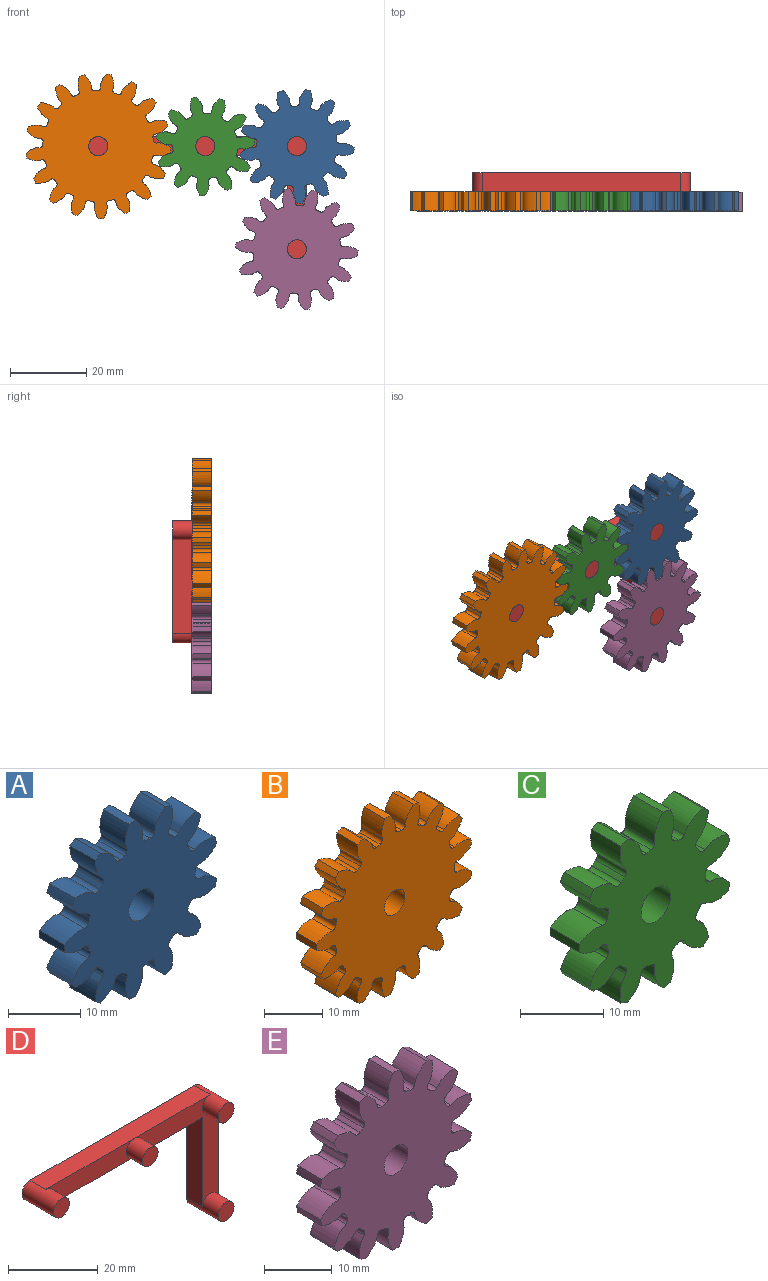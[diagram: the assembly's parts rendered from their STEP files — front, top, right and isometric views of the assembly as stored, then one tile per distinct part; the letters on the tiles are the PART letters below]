
ASSEMBLY  parts=5 mates=4
PART A: 81 faces, bbox 29.8x5x30 mm
  f0: extruded ~5x3.55mm, area 20.4mm2, adj f51,f52,f53,f54
  f1: cylinder r=10.5mm len=5mm, axis (0,1,0), area 4.2mm2, adj f52,f53,f54,f55
  f2: extruded ~5x3.55mm, area 20.4mm2, adj f3,f52,f53,f55
  f3: cylinder r=15mm len=5mm, axis (0,1,0), area 6.3mm2, adj f2,f4,f52,f53
  f4: extruded ~5x3.97mm, area 20.4mm2, adj f3,f52,f53,f56
  f5: cylinder r=10.5mm len=5mm, axis (0,1,0), area 4.2mm2, adj f52,f53,f56,f57
  f6: extruded ~5x3.23mm, area 20.4mm2, adj f7,f52,f53,f57
  f7: cylinder r=15mm len=5mm, axis (0,1,0), area 6.3mm2, adj f6,f8,f52,f53
  f8: extruded ~5x3.49mm, area 20.4mm2, adj f7,f52,f53,f58
  f9: cylinder r=10.5mm len=5mm, axis (0,1,0), area 4.2mm2, adj f52,f53,f58,f59
  f10: extruded ~5x3.94mm, area 20.4mm2, adj f11,f52,f53,f59
  f11: cylinder r=15mm len=5mm, axis (0,1,0), area 6.3mm2, adj f10,f12,f52,f53
  f12: extruded ~5x3.31mm, area 20.4mm2, adj f11,f52,f53,f60
  f13: cylinder r=10.5mm len=5mm, axis (0,1,0), area 4.2mm2, adj f52,f53,f60,f61
  f14: extruded ~5x3.74mm, area 20.4mm2, adj f15,f52,f53,f61
  f15: cylinder r=15mm len=5mm, axis (0,1,0), area 6.3mm2, adj f14,f16,f52,f53
  f16: extruded ~5x3.95mm, area 20.4mm2, adj f15,f52,f53,f62
  f17: cylinder r=10.5mm len=5mm, axis (0,1,0), area 4.2mm2, adj f52,f53,f62,f63
  f18: extruded ~5x2.93mm, area 20.4mm2, adj f19,f52,f53,f63
  f19: cylinder r=15mm len=5mm, axis (0,1,0), area 6.3mm2, adj f18,f20,f52,f53
  f20: extruded ~5x3.69mm, area 20.4mm2, adj f19,f52,f53,f64
  f21: cylinder r=10.5mm len=5mm, axis (0,1,0), area 4.2mm2, adj f52,f53,f64,f65
  f22: extruded ~5x3.84mm, area 20.4mm2, adj f23,f52,f53,f65
  f23: cylinder r=15mm len=5mm, axis (0,1,0), area 6.3mm2, adj f22,f24,f52,f53
  f24: extruded ~5x3.02mm, area 20.4mm2, adj f23,f52,f53,f66
  f25: cylinder r=10.5mm len=5mm, axis (0,1,0), area 4.2mm2, adj f52,f53,f66,f67
  f26: extruded ~5x3.87mm, area 20.4mm2, adj f27,f52,f53,f67
  f27: cylinder r=15mm len=5mm, axis (0,1,0), area 6.3mm2, adj f26,f28,f52,f53
  f28: extruded ~5x3.87mm, area 20.4mm2, adj f27,f52,f53,f68
  f29: cylinder r=10.5mm len=5mm, axis (0,1,0), area 4.2mm2, adj f52,f53,f68,f69
  f30: extruded ~5x3.02mm, area 20.4mm2, adj f31,f52,f53,f69
  f31: cylinder r=15mm len=5mm, axis (0,1,0), area 6.3mm2, adj f30,f32,f52,f53
  f32: extruded ~5x3.84mm, area 20.4mm2, adj f31,f52,f53,f70
  f33: cylinder r=10.5mm len=5mm, axis (0,1,0), area 4.2mm2, adj f52,f53,f70,f71
  f34: extruded ~5x3.69mm, area 20.4mm2, adj f35,f52,f53,f71
  f35: cylinder r=15mm len=5mm, axis (0,1,0), area 6.3mm2, adj f34,f36,f52,f53
  f36: extruded ~5x2.93mm, area 20.4mm2, adj f35,f52,f53,f72
  f37: cylinder r=10.5mm len=5mm, axis (0,1,0), area 4.2mm2, adj f52,f53,f72,f73
  f38: extruded ~5x3.95mm, area 20.4mm2, adj f39,f52,f53,f73
  f39: cylinder r=15mm len=5mm, axis (0,1,0), area 6.3mm2, adj f38,f40,f52,f53
  f40: extruded ~5x3.74mm, area 20.4mm2, adj f39,f52,f53,f74
  f41: cylinder r=10.5mm len=5mm, axis (0,1,0), area 4.2mm2, adj f52,f53,f74,f75
  f42: extruded ~5x3.31mm, area 20.4mm2, adj f43,f52,f53,f75
  f43: cylinder r=15mm len=5mm, axis (0,1,0), area 6.3mm2, adj f42,f44,f52,f53
  f44: extruded ~5x3.94mm, area 20.4mm2, adj f43,f52,f53,f76
  f45: cylinder r=10.5mm len=5mm, axis (0,1,0), area 4.2mm2, adj f52,f53,f76,f77
  f46: extruded ~5x3.49mm, area 20.4mm2, adj f47,f52,f53,f77
  f47: cylinder r=15mm len=5mm, axis (0,1,0), area 6.3mm2, adj f46,f48,f52,f53
  f48: extruded ~5x3.23mm, area 20.4mm2, adj f47,f52,f53,f78
  f49: cylinder r=10.5mm len=5mm, axis (0,1,0), area 4.2mm2, adj f52,f53,f78,f79
  f50: extruded ~5x3.97mm, area 20.4mm2, adj f51,f52,f53,f79
  f51: cylinder r=15mm len=5mm, axis (0,1,0), area 6.3mm2, adj f0,f50,f52,f53
  f52: plane 29.98x29.76mm, normal (0,-1,0), area 492.7mm2, adj f0,f1,f2,f3,f4,f5,f6,f7
  f53: plane 29.98x29.76mm, normal (0,1,0), area 492.7mm2, adj f0,f1,f2,f3,f4,f5,f6,f7
  f54: cylinder r=0.74mm len=5mm, axis (0,1,0), area 5.6mm2, adj f0,f1,f52,f53
  f55: cylinder r=0.74mm len=5mm, axis (0,1,0), area 5.6mm2, adj f1,f2,f52,f53
  f56: cylinder r=0.74mm len=5mm, axis (0,1,0), area 5.6mm2, adj f4,f5,f52,f53
  f57: cylinder r=0.74mm len=5mm, axis (0,1,0), area 5.6mm2, adj f5,f6,f52,f53
  f58: cylinder r=0.74mm len=5mm, axis (0,1,0), area 5.6mm2, adj f8,f9,f52,f53
  f59: cylinder r=0.74mm len=5mm, axis (0,1,0), area 5.6mm2, adj f9,f10,f52,f53
  f60: cylinder r=0.74mm len=5mm, axis (0,1,0), area 5.6mm2, adj f12,f13,f52,f53
  f61: cylinder r=0.74mm len=5mm, axis (0,1,0), area 5.6mm2, adj f13,f14,f52,f53
  f62: cylinder r=0.74mm len=5mm, axis (0,1,0), area 5.6mm2, adj f16,f17,f52,f53
  f63: cylinder r=0.74mm len=5mm, axis (0,1,0), area 5.6mm2, adj f17,f18,f52,f53
  f64: cylinder r=0.74mm len=5mm, axis (0,1,0), area 5.6mm2, adj f20,f21,f52,f53
  f65: cylinder r=0.74mm len=5mm, axis (0,1,0), area 5.6mm2, adj f21,f22,f52,f53
  f66: cylinder r=0.74mm len=5mm, axis (0,1,0), area 5.6mm2, adj f24,f25,f52,f53
  f67: cylinder r=0.74mm len=5mm, axis (0,1,0), area 5.6mm2, adj f25,f26,f52,f53
  f68: cylinder r=0.74mm len=5mm, axis (0,1,0), area 5.6mm2, adj f28,f29,f52,f53
  f69: cylinder r=0.74mm len=5mm, axis (0,1,0), area 5.6mm2, adj f29,f30,f52,f53
  f70: cylinder r=0.74mm len=5mm, axis (0,1,0), area 5.6mm2, adj f32,f33,f52,f53
  f71: cylinder r=0.74mm len=5mm, axis (0,1,0), area 5.6mm2, adj f33,f34,f52,f53
  f72: cylinder r=0.74mm len=5mm, axis (0,1,0), area 5.6mm2, adj f36,f37,f52,f53
  f73: cylinder r=0.74mm len=5mm, axis (0,1,0), area 5.6mm2, adj f37,f38,f52,f53
  f74: cylinder r=0.74mm len=5mm, axis (0,1,0), area 5.6mm2, adj f40,f41,f52,f53
  f75: cylinder r=0.74mm len=5mm, axis (0,1,0), area 5.6mm2, adj f41,f42,f52,f53
  f76: cylinder r=0.74mm len=5mm, axis (0,1,0), area 5.6mm2, adj f44,f45,f52,f53
  f77: cylinder r=0.74mm len=5mm, axis (0,1,0), area 5.6mm2, adj f45,f46,f52,f53
  f78: cylinder r=0.74mm len=5mm, axis (0,1,0), area 5.6mm2, adj f48,f49,f52,f53
  f79: cylinder r=0.74mm len=5mm, axis (0,1,0), area 5.6mm2, adj f49,f50,f52,f53
  f80: cylinder r=2.5mm len=5mm, axis (0,1,0), area 78.5mm2, adj f52,f53
PART B: 105 faces, bbox 37.8x5x38 mm
  f0: extruded ~5x3.6mm, area 20.3mm2, adj f67,f68,f69,f70
  f1: cylinder r=14.5mm len=5mm, axis (0,1,0), area 4.1mm2, adj f68,f69,f70,f71
  f2: extruded ~5x3.6mm, area 20.3mm2, adj f3,f68,f69,f71
  f3: cylinder r=19mm len=5mm, axis (0,1,0), area 6.7mm2, adj f2,f4,f68,f69
  f4: extruded ~5x3.96mm, area 20.3mm2, adj f3,f68,f69,f72
  f5: cylinder r=14.5mm len=5mm, axis (0,1,0), area 4.1mm2, adj f68,f69,f72,f73
  f6: extruded ~5x2.84mm, area 20.3mm2, adj f7,f68,f69,f73
  f7: cylinder r=19mm len=5mm, axis (0,1,0), area 6.7mm2, adj f6,f8,f68,f69
  f8: extruded ~5x3.77mm, area 20.3mm2, adj f7,f68,f69,f74
  f9: cylinder r=14.5mm len=5mm, axis (0,1,0), area 4.1mm2, adj f68,f69,f74,f75
  f10: extruded ~5x3.65mm, area 20.3mm2, adj f11,f68,f69,f75
  f11: cylinder r=19mm len=5mm, axis (0,1,0), area 6.7mm2, adj f10,f12,f68,f69
  f12: extruded ~5x3.08mm, area 20.3mm2, adj f11,f68,f69,f76
  f13: cylinder r=14.5mm len=5mm, axis (0,1,0), area 4.1mm2, adj f68,f69,f76,f77
  f14: extruded ~5x3.96mm, area 20.3mm2, adj f15,f68,f69,f77
  f15: cylinder r=19mm len=5mm, axis (0,1,0), area 6.7mm2, adj f14,f16,f68,f69
  f16: extruded ~5x3.44mm, area 20.3mm2, adj f15,f68,f69,f78
  f17: cylinder r=14.5mm len=5mm, axis (0,1,0), area 4.1mm2, adj f68,f69,f78,f79
  f18: extruded ~5x3.74mm, area 20.3mm2, adj f19,f68,f69,f79
  f19: cylinder r=19mm len=5mm, axis (0,1,0), area 6.7mm2, adj f18,f20,f68,f69
  f20: extruded ~5x3.92mm, area 20.3mm2, adj f19,f68,f69,f80
  f21: cylinder r=14.5mm len=5mm, axis (0,1,0), area 4.1mm2, adj f68,f69,f80,f81
  f22: extruded ~5x3.01mm, area 20.3mm2, adj f23,f68,f69,f81
  f23: cylinder r=19mm len=5mm, axis (0,1,0), area 6.7mm2, adj f22,f24,f68,f69
  f24: extruded ~5x3.87mm, area 20.3mm2, adj f23,f68,f69,f82
  f25: cylinder r=14.5mm len=5mm, axis (0,1,0), area 4.1mm2, adj f68,f69,f82,f83
  f26: extruded ~5x3.49mm, area 20.3mm2, adj f27,f68,f69,f83
  f27: cylinder r=19mm len=5mm, axis (0,1,0), area 6.7mm2, adj f26,f28,f68,f69
  f28: extruded ~5x3.3mm, area 20.3mm2, adj f27,f68,f69,f84
  f29: cylinder r=14.5mm len=5mm, axis (0,1,0), area 4.1mm2, adj f68,f69,f84,f85
  f30: extruded ~5x3.93mm, area 20.3mm2, adj f31,f68,f69,f85
  f31: cylinder r=19mm len=5mm, axis (0,1,0), area 6.7mm2, adj f30,f32,f68,f69
  f32: extruded ~5x3.24mm, area 20.3mm2, adj f31,f68,f69,f86
  f33: cylinder r=14.5mm len=5mm, axis (0,1,0), area 4.1mm2, adj f68,f69,f86,f87
  f34: extruded ~5x3.84mm, area 20.3mm2, adj f35,f68,f69,f87
  f35: cylinder r=19mm len=5mm, axis (0,1,0), area 6.7mm2, adj f34,f36,f68,f69
  f36: extruded ~5x3.84mm, area 20.3mm2, adj f35,f68,f69,f88
  f37: cylinder r=14.5mm len=5mm, axis (0,1,0), area 4.1mm2, adj f68,f69,f88,f89
  f38: extruded ~5x3.24mm, area 20.3mm2, adj f39,f68,f69,f89
  f39: cylinder r=19mm len=5mm, axis (0,1,0), area 6.7mm2, adj f38,f40,f68,f69
  f40: extruded ~5x3.93mm, area 20.3mm2, adj f39,f68,f69,f90
  f41: cylinder r=14.5mm len=5mm, axis (0,1,0), area 4.1mm2, adj f68,f69,f90,f91
  f42: extruded ~5x3.3mm, area 20.3mm2, adj f43,f68,f69,f91
  f43: cylinder r=19mm len=5mm, axis (0,1,0), area 6.7mm2, adj f42,f44,f68,f69
  f44: extruded ~5x3.49mm, area 20.3mm2, adj f43,f68,f69,f92
  f45: cylinder r=14.5mm len=5mm, axis (0,1,0), area 4.1mm2, adj f68,f69,f92,f93
  f46: extruded ~5x3.87mm, area 20.3mm2, adj f47,f68,f69,f93
  f47: cylinder r=19mm len=5mm, axis (0,1,0), area 6.7mm2, adj f46,f48,f68,f69
  f48: extruded ~5x3.01mm, area 20.3mm2, adj f47,f68,f69,f94
  f49: cylinder r=14.5mm len=5mm, axis (0,1,0), area 4.1mm2, adj f68,f69,f94,f95
  f50: extruded ~5x3.92mm, area 20.3mm2, adj f51,f68,f69,f95
  f51: cylinder r=19mm len=5mm, axis (0,1,0), area 6.7mm2, adj f50,f52,f68,f69
  f52: extruded ~5x3.74mm, area 20.3mm2, adj f51,f68,f69,f96
  f53: cylinder r=14.5mm len=5mm, axis (0,1,0), area 4.1mm2, adj f68,f69,f96,f97
  f54: extruded ~5x3.44mm, area 20.3mm2, adj f55,f68,f69,f97
  f55: cylinder r=19mm len=5mm, axis (0,1,0), area 6.7mm2, adj f54,f56,f68,f69
  f56: extruded ~5x3.96mm, area 20.3mm2, adj f55,f68,f69,f98
  f57: cylinder r=14.5mm len=5mm, axis (0,1,0), area 4.1mm2, adj f68,f69,f98,f99
  f58: extruded ~5x3.08mm, area 20.3mm2, adj f59,f68,f69,f99
  f59: cylinder r=19mm len=5mm, axis (0,1,0), area 6.7mm2, adj f58,f60,f68,f69
  f60: extruded ~5x3.65mm, area 20.3mm2, adj f59,f68,f69,f100
  f61: cylinder r=14.5mm len=5mm, axis (0,1,0), area 4.1mm2, adj f68,f69,f100,f101
  f62: extruded ~5x3.77mm, area 20.3mm2, adj f63,f68,f69,f101
  f63: cylinder r=19mm len=5mm, axis (0,1,0), area 6.7mm2, adj f62,f64,f68,f69
  f64: extruded ~5x2.84mm, area 20.3mm2, adj f63,f68,f69,f102
  f65: cylinder r=14.5mm len=5mm, axis (0,1,0), area 4.1mm2, adj f68,f69,f102,f103
  f66: extruded ~5x3.96mm, area 20.3mm2, adj f67,f68,f69,f103
  f67: cylinder r=19mm len=5mm, axis (0,1,0), area 6.7mm2, adj f0,f66,f68,f69
  f68: plane 37.98x37.82mm, normal (0,-1,0), area 865mm2, adj f0,f1,f2,f3,f4,f5,f6,f7
  f69: plane 37.98x37.82mm, normal (0,1,0), area 865mm2, adj f0,f1,f2,f3,f4,f5,f6,f7
  f70: cylinder r=0.75mm len=5mm, axis (0,1,0), area 5.7mm2, adj f0,f1,f68,f69
  f71: cylinder r=0.75mm len=5mm, axis (0,1,0), area 5.7mm2, adj f1,f2,f68,f69
  f72: cylinder r=0.75mm len=5mm, axis (0,1,0), area 5.7mm2, adj f4,f5,f68,f69
  f73: cylinder r=0.75mm len=5mm, axis (0,1,0), area 5.7mm2, adj f5,f6,f68,f69
  f74: cylinder r=0.75mm len=5mm, axis (0,1,0), area 5.7mm2, adj f8,f9,f68,f69
  f75: cylinder r=0.75mm len=5mm, axis (0,1,0), area 5.7mm2, adj f9,f10,f68,f69
  f76: cylinder r=0.75mm len=5mm, axis (0,1,0), area 5.7mm2, adj f12,f13,f68,f69
  f77: cylinder r=0.75mm len=5mm, axis (0,1,0), area 5.7mm2, adj f13,f14,f68,f69
  f78: cylinder r=0.75mm len=5mm, axis (0,1,0), area 5.7mm2, adj f16,f17,f68,f69
  f79: cylinder r=0.75mm len=5mm, axis (0,1,0), area 5.7mm2, adj f17,f18,f68,f69
  f80: cylinder r=0.75mm len=5mm, axis (0,1,0), area 5.7mm2, adj f20,f21,f68,f69
  f81: cylinder r=0.75mm len=5mm, axis (0,1,0), area 5.7mm2, adj f21,f22,f68,f69
  f82: cylinder r=0.75mm len=5mm, axis (0,1,0), area 5.7mm2, adj f24,f25,f68,f69
  f83: cylinder r=0.75mm len=5mm, axis (0,1,0), area 5.7mm2, adj f25,f26,f68,f69
  f84: cylinder r=0.75mm len=5mm, axis (0,1,0), area 5.7mm2, adj f28,f29,f68,f69
  f85: cylinder r=0.75mm len=5mm, axis (0,1,0), area 5.7mm2, adj f29,f30,f68,f69
  f86: cylinder r=0.75mm len=5mm, axis (0,1,0), area 5.7mm2, adj f32,f33,f68,f69
  f87: cylinder r=0.75mm len=5mm, axis (0,1,0), area 5.7mm2, adj f33,f34,f68,f69
  f88: cylinder r=0.75mm len=5mm, axis (0,1,0), area 5.7mm2, adj f36,f37,f68,f69
  f89: cylinder r=0.75mm len=5mm, axis (0,1,0), area 5.7mm2, adj f37,f38,f68,f69
  f90: cylinder r=0.75mm len=5mm, axis (0,1,0), area 5.7mm2, adj f40,f41,f68,f69
  f91: cylinder r=0.75mm len=5mm, axis (0,1,0), area 5.7mm2, adj f41,f42,f68,f69
  f92: cylinder r=0.75mm len=5mm, axis (0,1,0), area 5.7mm2, adj f44,f45,f68,f69
  f93: cylinder r=0.75mm len=5mm, axis (0,1,0), area 5.7mm2, adj f45,f46,f68,f69
  f94: cylinder r=0.75mm len=5mm, axis (0,1,0), area 5.7mm2, adj f48,f49,f68,f69
  f95: cylinder r=0.75mm len=5mm, axis (0,1,0), area 5.7mm2, adj f49,f50,f68,f69
  f96: cylinder r=0.75mm len=5mm, axis (0,1,0), area 5.7mm2, adj f52,f53,f68,f69
  f97: cylinder r=0.75mm len=5mm, axis (0,1,0), area 5.7mm2, adj f53,f54,f68,f69
  f98: cylinder r=0.75mm len=5mm, axis (0,1,0), area 5.7mm2, adj f56,f57,f68,f69
  f99: cylinder r=0.75mm len=5mm, axis (0,1,0), area 5.7mm2, adj f57,f58,f68,f69
  f100: cylinder r=0.75mm len=5mm, axis (0,1,0), area 5.7mm2, adj f60,f61,f68,f69
  f101: cylinder r=0.75mm len=5mm, axis (0,1,0), area 5.7mm2, adj f61,f62,f68,f69
  f102: cylinder r=0.75mm len=5mm, axis (0,1,0), area 5.7mm2, adj f64,f65,f68,f69
  f103: cylinder r=0.75mm len=5mm, axis (0,1,0), area 5.7mm2, adj f65,f66,f68,f69
  f104: cylinder r=2.5mm len=5mm, axis (0,1,0), area 78.5mm2, adj f68,f69
PART C: 69 faces, bbox 25.7x5x26 mm
  f0: extruded ~5x3.51mm, area 20.6mm2, adj f43,f44,f45,f46
  f1: cylinder r=8.5mm len=5mm, axis (0,1,0), area 4.2mm2, adj f44,f45,f46,f47
  f2: extruded ~5x3.51mm, area 20.6mm2, adj f3,f44,f45,f47
  f3: cylinder r=13mm len=5mm, axis (0,1,0), area 6mm2, adj f2,f4,f44,f45
  f4: extruded ~5x3.98mm, area 20.6mm2, adj f3,f44,f45,f48
  f5: cylinder r=8.5mm len=5mm, axis (0,1,0), area 4.2mm2, adj f44,f45,f48,f49
  f6: extruded ~5x3.5mm, area 20.6mm2, adj f7,f44,f45,f49
  f7: cylinder r=13mm len=5mm, axis (0,1,0), area 6mm2, adj f6,f8,f44,f45
  f8: extruded ~5x3.19mm, area 20.6mm2, adj f7,f44,f45,f50
  f9: cylinder r=8.5mm len=5mm, axis (0,1,0), area 4.2mm2, adj f44,f45,f50,f51
  f10: extruded ~5x3.98mm, area 20.6mm2, adj f11,f44,f45,f51
  f11: cylinder r=13mm len=5mm, axis (0,1,0), area 6mm2, adj f10,f12,f44,f45
  f12: extruded ~5x3.75mm, area 20.6mm2, adj f11,f44,f45,f52
  f13: cylinder r=8.5mm len=5mm, axis (0,1,0), area 4.2mm2, adj f44,f45,f52,f53
  f14: extruded ~5x3.2mm, area 20.6mm2, adj f15,f44,f45,f53
  f15: cylinder r=13mm len=5mm, axis (0,1,0), area 6mm2, adj f14,f16,f44,f45
  f16: extruded ~5x3.9mm, area 20.6mm2, adj f15,f44,f45,f54
  f17: cylinder r=8.5mm len=5mm, axis (0,1,0), area 4.2mm2, adj f44,f45,f54,f55
  f18: extruded ~5x3.74mm, area 20.6mm2, adj f19,f44,f45,f55
  f19: cylinder r=13mm len=5mm, axis (0,1,0), area 6mm2, adj f18,f20,f44,f45
  f20: extruded ~5x2.83mm, area 20.6mm2, adj f19,f44,f45,f56
  f21: cylinder r=8.5mm len=5mm, axis (0,1,0), area 4.2mm2, adj f44,f45,f56,f57
  f22: extruded ~5x3.9mm, area 20.6mm2, adj f23,f44,f45,f57
  f23: cylinder r=13mm len=5mm, axis (0,1,0), area 6mm2, adj f22,f24,f44,f45
  f24: extruded ~5x3.9mm, area 20.6mm2, adj f23,f44,f45,f58
  f25: cylinder r=8.5mm len=5mm, axis (0,1,0), area 4.2mm2, adj f44,f45,f58,f59
  f26: extruded ~5x2.83mm, area 20.6mm2, adj f27,f44,f45,f59
  f27: cylinder r=13mm len=5mm, axis (0,1,0), area 6mm2, adj f26,f28,f44,f45
  f28: extruded ~5x3.74mm, area 20.6mm2, adj f27,f44,f45,f60
  f29: cylinder r=8.5mm len=5mm, axis (0,1,0), area 4.2mm2, adj f44,f45,f60,f61
  f30: extruded ~5x3.9mm, area 20.6mm2, adj f31,f44,f45,f61
  f31: cylinder r=13mm len=5mm, axis (0,1,0), area 6mm2, adj f30,f32,f44,f45
  f32: extruded ~5x3.2mm, area 20.6mm2, adj f31,f44,f45,f62
  f33: cylinder r=8.5mm len=5mm, axis (0,1,0), area 4.2mm2, adj f44,f45,f62,f63
  f34: extruded ~5x3.75mm, area 20.6mm2, adj f35,f44,f45,f63
  f35: cylinder r=13mm len=5mm, axis (0,1,0), area 6mm2, adj f34,f36,f44,f45
  f36: extruded ~5x3.98mm, area 20.6mm2, adj f35,f44,f45,f64
  f37: cylinder r=8.5mm len=5mm, axis (0,1,0), area 4.2mm2, adj f44,f45,f64,f65
  f38: extruded ~5x3.19mm, area 20.6mm2, adj f39,f44,f45,f65
  f39: cylinder r=13mm len=5mm, axis (0,1,0), area 6mm2, adj f38,f40,f44,f45
  f40: extruded ~5x3.5mm, area 20.6mm2, adj f39,f44,f45,f66
  f41: cylinder r=8.5mm len=5mm, axis (0,1,0), area 4.2mm2, adj f44,f45,f66,f67
  f42: extruded ~5x3.98mm, area 20.6mm2, adj f43,f44,f45,f67
  f43: cylinder r=13mm len=5mm, axis (0,1,0), area 6mm2, adj f0,f42,f44,f45
  f44: plane 25.96x25.7mm, normal (0,-1,0), area 344.7mm2, adj f0,f1,f2,f3,f4,f5,f6,f7
  f45: plane 25.96x25.7mm, normal (0,1,0), area 344.7mm2, adj f0,f1,f2,f3,f4,f5,f6,f7
  f46: cylinder r=0.72mm len=5mm, axis (0,1,0), area 5.4mm2, adj f0,f1,f44,f45
  f47: cylinder r=0.72mm len=5mm, axis (0,1,0), area 5.4mm2, adj f1,f2,f44,f45
  f48: cylinder r=0.72mm len=5mm, axis (0,1,0), area 5.4mm2, adj f4,f5,f44,f45
  f49: cylinder r=0.72mm len=5mm, axis (0,1,0), area 5.4mm2, adj f5,f6,f44,f45
  f50: cylinder r=0.72mm len=5mm, axis (0,1,0), area 5.4mm2, adj f8,f9,f44,f45
  f51: cylinder r=0.72mm len=5mm, axis (0,1,0), area 5.4mm2, adj f9,f10,f44,f45
  f52: cylinder r=0.72mm len=5mm, axis (0,1,0), area 5.4mm2, adj f12,f13,f44,f45
  f53: cylinder r=0.72mm len=5mm, axis (0,1,0), area 5.4mm2, adj f13,f14,f44,f45
  f54: cylinder r=0.72mm len=5mm, axis (0,1,0), area 5.4mm2, adj f16,f17,f44,f45
  f55: cylinder r=0.72mm len=5mm, axis (0,1,0), area 5.4mm2, adj f17,f18,f44,f45
  f56: cylinder r=0.72mm len=5mm, axis (0,1,0), area 5.4mm2, adj f20,f21,f44,f45
  f57: cylinder r=0.72mm len=5mm, axis (0,1,0), area 5.4mm2, adj f21,f22,f44,f45
  f58: cylinder r=0.72mm len=5mm, axis (0,1,0), area 5.4mm2, adj f24,f25,f44,f45
  f59: cylinder r=0.72mm len=5mm, axis (0,1,0), area 5.4mm2, adj f25,f26,f44,f45
  f60: cylinder r=0.72mm len=5mm, axis (0,1,0), area 5.4mm2, adj f28,f29,f44,f45
  f61: cylinder r=0.72mm len=5mm, axis (0,1,0), area 5.4mm2, adj f29,f30,f44,f45
  f62: cylinder r=0.72mm len=5mm, axis (0,1,0), area 5.4mm2, adj f32,f33,f44,f45
  f63: cylinder r=0.72mm len=5mm, axis (0,1,0), area 5.4mm2, adj f33,f34,f44,f45
  f64: cylinder r=0.72mm len=5mm, axis (0,1,0), area 5.4mm2, adj f36,f37,f44,f45
  f65: cylinder r=0.72mm len=5mm, axis (0,1,0), area 5.4mm2, adj f37,f38,f44,f45
  f66: cylinder r=0.72mm len=5mm, axis (0,1,0), area 5.4mm2, adj f40,f41,f44,f45
  f67: cylinder r=0.72mm len=5mm, axis (0,1,0), area 5.4mm2, adj f41,f42,f44,f45
  f68: cylinder r=2.5mm len=5mm, axis (0,1,0), area 78.5mm2, adj f44,f45
PART D: 15 faces, bbox 57x10x32 mm
  f0: plane 29.5x26.5mm, normal (0,-1,0), area 214.4mm2, adj f3,f4,f5,f6,f7,f8,f11
  f1: plane 28x5mm, normal (0,-1,0), area 120.4mm2, adj f2,f3,f8,f11
  f2: cylinder r=2.5mm len=10mm, axis (0,1,0), area 117.8mm2, adj f1,f3,f8,f9,f10
  f3: plane 49.5x5mm, normal (0,0,-1), area 247.5mm2, adj f0,f1,f2,f4,f9
  f4: plane 24.5x5mm, normal (-1,0,0), area 122.5mm2, adj f0,f3,f5,f9
  f5: cylinder r=2.5mm len=10mm, axis (0,1,0), area 117.8mm2, adj f0,f4,f6,f9,f14
  f6: plane 27x5mm, normal (1,0,0), area 135mm2, adj f0,f5,f7,f9
  f7: cylinder r=2.5mm len=10mm, axis (0,1,0), area 98.2mm2, adj f0,f6,f8,f9,f13
  f8: plane 52x5mm, normal (0,0,1), area 260mm2, adj f0,f1,f2,f7,f9
  f9: plane 57x32mm, normal (0,1,0), area 413.3mm2, adj f2,f3,f4,f5,f6,f7,f8
  f10: plane 5x5mm, normal (0,-1,0), area 19.6mm2, adj f2
  f11: cylinder r=2.5mm len=5mm, axis (0,1,0), area 78.5mm2, adj f0,f1,f12
  f12: plane 5x5mm, normal (0,-1,0), area 19.6mm2, adj f11
  f13: plane 5x5mm, normal (0,-1,0), area 19.6mm2, adj f7
  f14: plane 5x5mm, normal (0,-1,0), area 19.6mm2, adj f5
PART E: 87 faces, bbox 31.5x5x32 mm
  f0: extruded ~5x3.56mm, area 20.4mm2, adj f55,f56,f57,f58
  f1: cylinder r=11.5mm len=5mm, axis (0,1,0), area 4.2mm2, adj f56,f57,f58,f59
  f2: extruded ~5x3.56mm, area 20.4mm2, adj f3,f56,f57,f59
  f3: cylinder r=16mm len=5mm, axis (0,1,0), area 6.5mm2, adj f2,f4,f56,f57
  f4: extruded ~5x3.97mm, area 20.4mm2, adj f3,f56,f57,f60
  f5: cylinder r=11.5mm len=5mm, axis (0,1,0), area 4.2mm2, adj f56,f57,f60,f61
  f6: extruded ~5x3.12mm, area 20.4mm2, adj f7,f56,f57,f61
  f7: cylinder r=16mm len=5mm, axis (0,1,0), area 6.5mm2, adj f6,f8,f56,f57
  f8: extruded ~5x3.59mm, area 20.4mm2, adj f7,f56,f57,f62
  f9: cylinder r=11.5mm len=5mm, axis (0,1,0), area 4.2mm2, adj f56,f57,f62,f63
  f10: extruded ~5x3.87mm, area 20.4mm2, adj f11,f56,f57,f63
  f11: cylinder r=16mm len=5mm, axis (0,1,0), area 6.5mm2, adj f10,f12,f56,f57
  f12: extruded ~5x3.09mm, area 20.4mm2, adj f11,f56,f57,f64
  f13: cylinder r=11.5mm len=5mm, axis (0,1,0), area 4.2mm2, adj f56,f57,f64,f65
  f14: extruded ~5x3.86mm, area 20.4mm2, adj f15,f56,f57,f65
  f15: cylinder r=16mm len=5mm, axis (0,1,0), area 6.5mm2, adj f14,f16,f56,f57
  f16: extruded ~5x3.86mm, area 20.4mm2, adj f15,f56,f57,f66
  f17: cylinder r=11.5mm len=5mm, axis (0,1,0), area 4.2mm2, adj f56,f57,f66,f67
  f18: extruded ~5x3.09mm, area 20.4mm2, adj f19,f56,f57,f67
  f19: cylinder r=16mm len=5mm, axis (0,1,0), area 6.5mm2, adj f18,f20,f56,f57
  f20: extruded ~5x3.87mm, area 20.4mm2, adj f19,f56,f57,f68
  f21: cylinder r=11.5mm len=5mm, axis (0,1,0), area 4.2mm2, adj f56,f57,f68,f69
  f22: extruded ~5x3.59mm, area 20.4mm2, adj f23,f56,f57,f69
  f23: cylinder r=16mm len=5mm, axis (0,1,0), area 6.5mm2, adj f22,f24,f56,f57
  f24: extruded ~5x3.12mm, area 20.4mm2, adj f23,f56,f57,f70
  f25: cylinder r=11.5mm len=5mm, axis (0,1,0), area 4.2mm2, adj f56,f57,f70,f71
  f26: extruded ~5x3.97mm, area 20.4mm2, adj f27,f56,f57,f71
  f27: cylinder r=16mm len=5mm, axis (0,1,0), area 6.5mm2, adj f26,f28,f56,f57
  f28: extruded ~5x3.56mm, area 20.4mm2, adj f27,f56,f57,f72
  f29: cylinder r=11.5mm len=5mm, axis (0,1,0), area 4.2mm2, adj f56,f57,f72,f73
  f30: extruded ~5x3.56mm, area 20.4mm2, adj f31,f56,f57,f73
  f31: cylinder r=16mm len=5mm, axis (0,1,0), area 6.5mm2, adj f30,f32,f56,f57
  f32: extruded ~5x3.97mm, area 20.4mm2, adj f31,f56,f57,f74
  f33: cylinder r=11.5mm len=5mm, axis (0,1,0), area 4.2mm2, adj f56,f57,f74,f75
  f34: extruded ~5x3.12mm, area 20.4mm2, adj f35,f56,f57,f75
  f35: cylinder r=16mm len=5mm, axis (0,1,0), area 6.5mm2, adj f34,f36,f56,f57
  f36: extruded ~5x3.59mm, area 20.4mm2, adj f35,f56,f57,f76
  f37: cylinder r=11.5mm len=5mm, axis (0,1,0), area 4.2mm2, adj f56,f57,f76,f77
  f38: extruded ~5x3.87mm, area 20.4mm2, adj f39,f56,f57,f77
  f39: cylinder r=16mm len=5mm, axis (0,1,0), area 6.5mm2, adj f38,f40,f56,f57
  f40: extruded ~5x3.09mm, area 20.4mm2, adj f39,f56,f57,f78
  f41: cylinder r=11.5mm len=5mm, axis (0,1,0), area 4.2mm2, adj f56,f57,f78,f79
  f42: extruded ~5x3.86mm, area 20.4mm2, adj f43,f56,f57,f79
  f43: cylinder r=16mm len=5mm, axis (0,1,0), area 6.5mm2, adj f42,f44,f56,f57
  f44: extruded ~5x3.86mm, area 20.4mm2, adj f43,f56,f57,f80
  f45: cylinder r=11.5mm len=5mm, axis (0,1,0), area 4.2mm2, adj f56,f57,f80,f81
  f46: extruded ~5x3.09mm, area 20.4mm2, adj f47,f56,f57,f81
  f47: cylinder r=16mm len=5mm, axis (0,1,0), area 6.5mm2, adj f46,f48,f56,f57
  f48: extruded ~5x3.87mm, area 20.4mm2, adj f47,f56,f57,f82
  f49: cylinder r=11.5mm len=5mm, axis (0,1,0), area 4.2mm2, adj f56,f57,f82,f83
  f50: extruded ~5x3.59mm, area 20.4mm2, adj f51,f56,f57,f83
  f51: cylinder r=16mm len=5mm, axis (0,1,0), area 6.5mm2, adj f50,f52,f56,f57
  f52: extruded ~5x3.12mm, area 20.4mm2, adj f51,f56,f57,f84
  f53: cylinder r=11.5mm len=5mm, axis (0,1,0), area 4.2mm2, adj f56,f57,f84,f85
  f54: extruded ~5x3.97mm, area 20.4mm2, adj f55,f56,f57,f85
  f55: cylinder r=16mm len=5mm, axis (0,1,0), area 6.5mm2, adj f0,f54,f56,f57
  f56: plane 32.04x31.52mm, normal (0,-1,0), area 576.2mm2, adj f0,f1,f2,f3,f4,f5,f6,f7
  f57: plane 32.04x31.52mm, normal (0,1,0), area 576.2mm2, adj f0,f1,f2,f3,f4,f5,f6,f7
  f58: cylinder r=0.74mm len=5mm, axis (0,1,0), area 5.6mm2, adj f0,f1,f56,f57
  f59: cylinder r=0.74mm len=5mm, axis (0,1,0), area 5.6mm2, adj f1,f2,f56,f57
  f60: cylinder r=0.74mm len=5mm, axis (0,1,0), area 5.6mm2, adj f4,f5,f56,f57
  f61: cylinder r=0.74mm len=5mm, axis (0,1,0), area 5.6mm2, adj f5,f6,f56,f57
  f62: cylinder r=0.74mm len=5mm, axis (0,1,0), area 5.6mm2, adj f8,f9,f56,f57
  f63: cylinder r=0.74mm len=5mm, axis (0,1,0), area 5.6mm2, adj f9,f10,f56,f57
  f64: cylinder r=0.74mm len=5mm, axis (0,1,0), area 5.6mm2, adj f12,f13,f56,f57
  f65: cylinder r=0.74mm len=5mm, axis (0,1,0), area 5.6mm2, adj f13,f14,f56,f57
  f66: cylinder r=0.74mm len=5mm, axis (0,1,0), area 5.6mm2, adj f16,f17,f56,f57
  f67: cylinder r=0.74mm len=5mm, axis (0,1,0), area 5.6mm2, adj f17,f18,f56,f57
  f68: cylinder r=0.74mm len=5mm, axis (0,1,0), area 5.6mm2, adj f20,f21,f56,f57
  f69: cylinder r=0.74mm len=5mm, axis (0,1,0), area 5.6mm2, adj f21,f22,f56,f57
  f70: cylinder r=0.74mm len=5mm, axis (0,1,0), area 5.6mm2, adj f24,f25,f56,f57
  f71: cylinder r=0.74mm len=5mm, axis (0,1,0), area 5.6mm2, adj f25,f26,f56,f57
  f72: cylinder r=0.74mm len=5mm, axis (0,1,0), area 5.6mm2, adj f28,f29,f56,f57
  f73: cylinder r=0.74mm len=5mm, axis (0,1,0), area 5.6mm2, adj f29,f30,f56,f57
  f74: cylinder r=0.74mm len=5mm, axis (0,1,0), area 5.6mm2, adj f32,f33,f56,f57
  f75: cylinder r=0.74mm len=5mm, axis (0,1,0), area 5.6mm2, adj f33,f34,f56,f57
  f76: cylinder r=0.74mm len=5mm, axis (0,1,0), area 5.6mm2, adj f36,f37,f56,f57
  f77: cylinder r=0.74mm len=5mm, axis (0,1,0), area 5.6mm2, adj f37,f38,f56,f57
  f78: cylinder r=0.74mm len=5mm, axis (0,1,0), area 5.6mm2, adj f40,f41,f56,f57
  f79: cylinder r=0.74mm len=5mm, axis (0,1,0), area 5.6mm2, adj f41,f42,f56,f57
  f80: cylinder r=0.74mm len=5mm, axis (0,1,0), area 5.6mm2, adj f44,f45,f56,f57
  f81: cylinder r=0.74mm len=5mm, axis (0,1,0), area 5.6mm2, adj f45,f46,f56,f57
  f82: cylinder r=0.74mm len=5mm, axis (0,1,0), area 5.6mm2, adj f48,f49,f56,f57
  f83: cylinder r=0.74mm len=5mm, axis (0,1,0), area 5.6mm2, adj f49,f50,f56,f57
  f84: cylinder r=0.74mm len=5mm, axis (0,1,0), area 5.6mm2, adj f52,f53,f56,f57
  f85: cylinder r=0.74mm len=5mm, axis (0,1,0), area 5.6mm2, adj f53,f54,f56,f57
  f86: cylinder r=2.5mm len=5mm, axis (0,1,0), area 78.5mm2, adj f56,f57
PLACE A rot(axis=(0,-1,0),9.9deg) t=(52,-5,0)mm
PLACE B rot(axis=(0,-1,0),176.9deg) t=(0,-5,0)mm
PLACE C rot(axis=(0,-1,0),119.3deg) t=(28,-5,0)mm
PLACE D at identity
PLACE E rot(axis=(0,-1,0),60.6deg) t=(52,-5,-27)mm
MATE revolute A.f3 <-> D.f7  axis (0,-1,0) through (52,-10,0)mm
MATE revolute C.f3 <-> D.f11  axis (0,-1,0) through (28,-10,0)mm
MATE revolute D.f5 <-> E.f37  axis (0,-1,0) through (52,-10,-27)mm
MATE revolute B.f3 <-> D.f2  axis (0,-1,0) through (0,-10,0)mm
